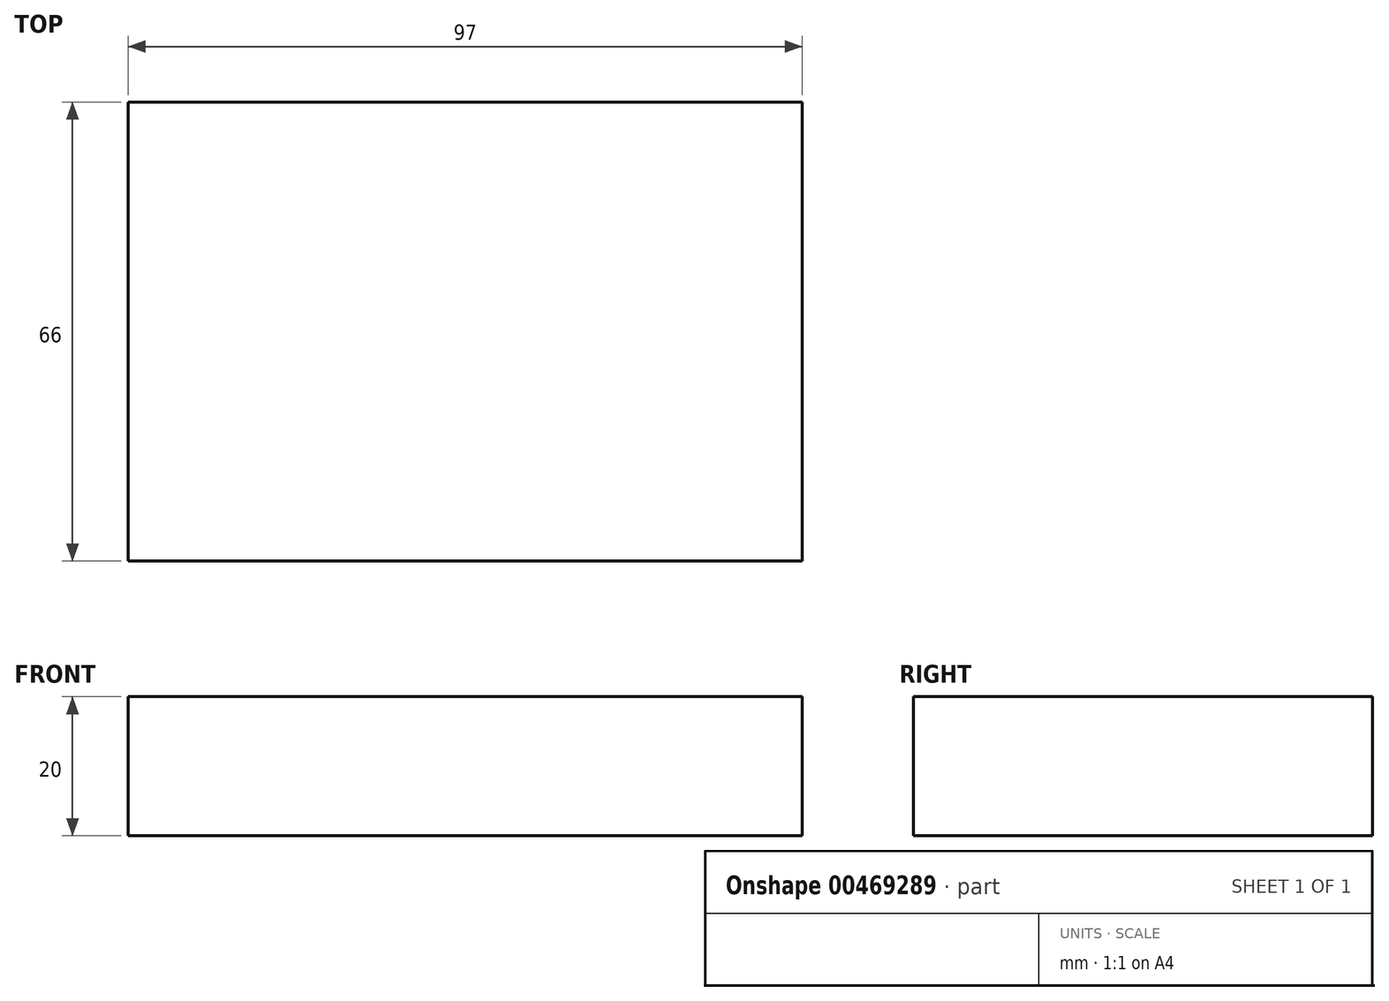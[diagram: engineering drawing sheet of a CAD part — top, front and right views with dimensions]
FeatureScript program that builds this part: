
annotation { "Feature Type Name" : "Feature", "Feature Type Description" : "" }
export const myFeature = defineFeature(function(context is Context, id is Id, definition is map)
    precondition{}
    {
        {
            var Q0;
            Q0=qCreatedBy(makeId("Top.planeOp"),FACE);
            var sketch = newSketch(context, id + "F0", { "sketchPlane" : qUnion([Q0])});
            skLineSegment(sketch, "E0.bottom", {"start": v(-48.5, 33) * mm, "end": v(48.5, 33) * mm});
            skLineSegment(sketch, "E0.top", {"start": v(-48.5, -33) * mm, "end": v(48.5, -33) * mm});
            skLineSegment(sketch, "E0.left", {"start": v(-48.5, 33) * mm, "end": v(-48.5, -33) * mm});
            skLineSegment(sketch, "E0.right", {"start": v(48.5, 33) * mm, "end": v(48.5, -33) * mm});
            skPoint(sketch, "E0.middle", {"position": v(0, 0) * mm});
            skSolve(sketch);
        }
        {
            var Q0;
            Q0=makeQuery(id+"F0.imprint","IMPRINT",FACE,{"disambiguationData":[TD([[makeQuery(id+"F0.imprint","IMPRINT",EDGE,{"derivedFrom":sQuery(id+"F0.wireOp",EDGE,"E0.bottom")}),-1.0]])]});
            extrude(context, id + "F1", {"entities" : qUnion([Q0]), "depth" : 20 * mm, "offsetDistance" : 25 * mm});
        }
    });
